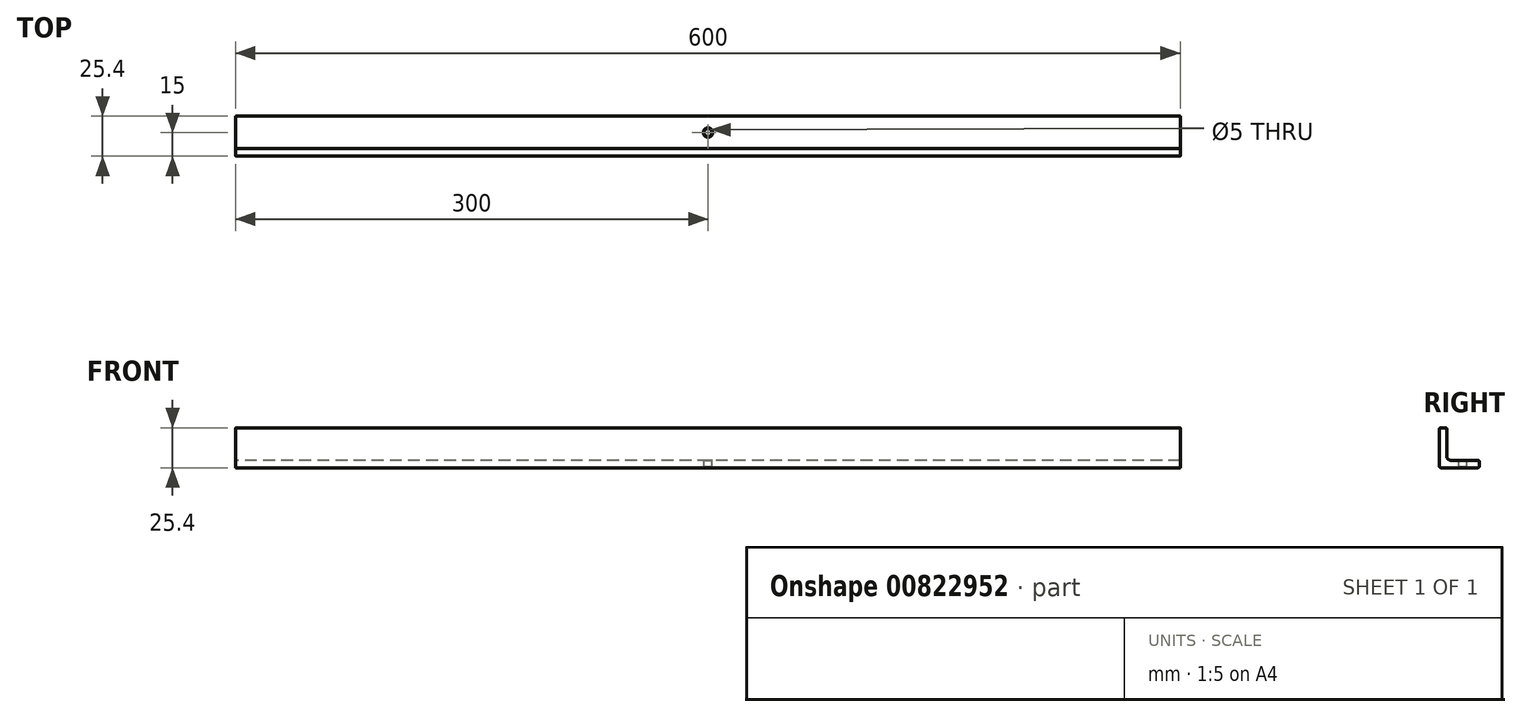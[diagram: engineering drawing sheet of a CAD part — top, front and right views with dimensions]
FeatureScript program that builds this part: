
annotation { "Feature Type Name" : "Feature", "Feature Type Description" : "" }
export const myFeature = defineFeature(function(context is Context, id is Id, definition is map)
    precondition{}
    {
        {
            var Q0;
            Q0=qCreatedBy(makeId("Right.planeOp"),FACE);
            var sketch = newSketch(context, id + "F0", { "sketchPlane" : qUnion([Q0])});
            skLineSegment(sketch, "E0", {"start": v(0, 0) * mm, "end": v(25.4, 0) * mm});
            skLineSegment(sketch, "E1", {"start": v(0, 0) * mm, "end": v(0, 25.4) * mm});
            skLineSegment(sketch, "E2", {"start": v(0, 25.4) * mm, "end": v(4.76, 25.4) * mm});
            skLineSegment(sketch, "E3", {"start": v(4.76, 25.4) * mm, "end": v(4.76, 4.76) * mm});
            skLineSegment(sketch, "E4", {"start": v(4.76, 4.76) * mm, "end": v(25.4, 4.76) * mm});
            skLineSegment(sketch, "E5", {"start": v(25.4, 4.76) * mm, "end": v(25.4, 0) * mm});
            skSolve(sketch);
        }
        {
            var Q0;
            Q0=qSketchRegion(id+"F0",true);
            extrude(context, id + "F1", {"entities" : qUnion([Q0]), "endBound" : BoundingType.SYMMETRIC, "depth" : 600 * mm, "offsetDistance" : 25 * mm});
        }
        {
            var Q0;
            Q0=makeQuery(id+"F1.opExtrude","SWEPT_EDGE",EDGE,{"disambiguationData":[OSD([sQuery(id+"F0.wireOp",EDGE,"E1"),sQuery(id+"F0.wireOp",EDGE,"E2")])]});
            var Q1;
            Q1=makeQuery(id+"F1.opExtrude","SWEPT_EDGE",EDGE,{"disambiguationData":[OSD([sQuery(id+"F0.wireOp",EDGE,"E2"),sQuery(id+"F0.wireOp",EDGE,"E3")])]});
            var Q2;
            Q2=makeQuery(id+"F1.opExtrude","SWEPT_EDGE",EDGE,{"disambiguationData":[OSD([sQuery(id+"F0.wireOp",EDGE,"E0"),sQuery(id+"F0.wireOp",EDGE,"E1")])]});
            var Q3;
            Q3=makeQuery(id+"F1.opExtrude","SWEPT_EDGE",EDGE,{"disambiguationData":[OSD([sQuery(id+"F0.wireOp",EDGE,"E4"),sQuery(id+"F0.wireOp",EDGE,"E5")])]});
            var Q4;
            Q4=makeQuery(id+"F1.opExtrude","SWEPT_EDGE",EDGE,{"disambiguationData":[OSD([sQuery(id+"F0.wireOp",EDGE,"E0"),sQuery(id+"F0.wireOp",EDGE,"E5")])]});
            fillet(context, id + "F2", {"entities" : qUnion([Q0, Q1, Q2, Q3, Q4]), "radius" : 1 * mm, "tangentPropagation" : true, "allowEdgeOverflow" : false});
        }
        {
            var Q0;
            Q0=makeQuery(id+"F1.opExtrude","SWEPT_EDGE",EDGE,{"disambiguationData":[OSD([sQuery(id+"F0.wireOp",EDGE,"E3"),sQuery(id+"F0.wireOp",EDGE,"E4")])]});
            fillet(context, id + "F3", {"entities" : qUnion([Q0]), "radius" : (3 * 25.4 / 16 / 2) * mm, "tangentPropagation" : true, "allowEdgeOverflow" : false});
        }
        {
            var Q0;
            Q0=makeQuery(id+"F1.opExtrude","SWEPT_FACE",FACE,{"disambiguationData":[OSD([sQuery(id+"F0.wireOp",EDGE,"E4")])]});
            var sketch = newSketch(context, id + "F4", { "sketchPlane" : qUnion([Q0])});
            skLineSegment(sketch, "E6", {"start": v(0, 0) * mm, "end": v(0, 15) * mm, "construction": true});
            skCircle(sketch, "E7", {"center": v(0, 15) * mm, "radius": 2.5 * mm});
            skSolve(sketch);
        }
        {
            var Q0;
            Q0 = qSketchRegion(id + "F4", true);
            extrude(context, id + "F5", {"entities" : qUnion([Q0]), "operationType" : NewBodyOperationType.REMOVE, "oppositeDirection" : true, "depth" : 25 * mm, "offsetDistance" : 25 * mm});
        }
        {
            var Q0;
            Q0=makeQuery(id+"F5.boolean.opBoolean","COPY",FACE,{"derivedFrom":makeQuery(id+"F5.opExtrude","SWEPT_FACE",FACE,{"disambiguationData":[OSD([sQuery(id+"F4.wireOp",EDGE,"E7")])]})});
            chamfer(context, id + "F6", {"entities" : qUnion([Q0]), "width" : 0.5 * mm, "tangentPropagation" : true});
        }
    });
